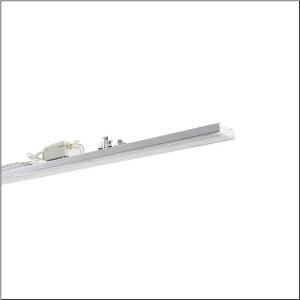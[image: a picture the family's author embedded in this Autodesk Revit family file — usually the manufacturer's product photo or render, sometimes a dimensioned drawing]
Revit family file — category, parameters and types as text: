
# Revit family: licross_r__21_recessed_mo_52tl11mn4a5g_bccd
name_source: partatom
category: Lighting Fixtures
units: mm (PartAtom-declared; Revit-internal decimal feet)

## family parameters
Cut with Voids When Loaded = No
Host = Face
Light Source = No
Part Type = Normal
Room Calculation Point = No
Round Connector Dimension = Use Diameter
Shared = No

## types (1)
- --- (1 x LED, 10830 lm, 60.5 W, 4000K)
    Apparent Load = 61 VA
    CIE Flux Codes = 89 96 99 100 100
    Color Rendering = 80
    Color Temperature = 4000K
    Default Elevation = 1800 mm
    Description = Licross® 21 Recessed MO, luminaire insert, of sheet steel, galvanised, coil coated, white, length: 1.500mm, width: 66mm, height: 67mm, LED rated luminous flux: 10.820lm, light colour: 840, control gear: ON/OFF Multilumen, with plug, 3-pole, with phase selection, mains connection: 220..240V, AC, 50/60Hz, rated input power: 61W, halogen-free wiring, primary light control with lens, of plastic, primary optical cover: cover, of PMMA, light emission: direct distribution, primary light characteristic: symmetric, protection rating (complete): IP40, insulation class (complete): insulation class I (protective earthing), certification: CE, ENEC, VDE, UKCA, protection symbol: D if used in an environment without relevant dust loads with corresponding accessories, impact resistance: IK06, permissible ambient temperature for indoor applications: -35..+40°C, corresponds to IFS (International Featured Standards) requirements for safety and quality in the food industry, reducing of maximum allowable ambient temperature of 5°C with ceiling mounting, LABS conformity tested according to VDMA 24364:2018-05, packaging unit: 1 piece
    Height = 58 mm
    Lamp = 1 x LED
    Lamp Light Flux = 10830 lm
    Lamp Power = 60.5 W
    Lamp count = 1
    Length = 1500 mm
    Luminous efficacy = 179 lm/W
    Manufacturer = Siteco
    ModVariant = No
    Model = 52TL11MN4A5G
    Mounting Place = Ceiling
    Mounting Type = Pendant
    Number of Poles = 1
    OnlyDefault = Yes
    Power Factor = 1
    Product Name = Licross® 21 Recessed MO
    Product group = luminaire insert
    ProductGroupID = 901
    Protection Class = Protection class I
    Protection Degree = IP 40
    RLX_Detail_Level = 1
    RLX_Emergency_Light_Flux = 0 lm
    RLX_Emergency_Type = 0
    RLX_Emergency_Type_DB = No
    RlxData = <blob elided: 22169 chars, md5=3a20e823>
    Socket = socket
    Standby Power = 0 W
    System Light Flux = 10830 lm
    System Power = 61 W
    Type Comments = factory setting: luminous flux: 100 % | (A | C | E) | 140 mA
    Type Image = l_1296930.jpg
    URL = http://relux.com
    VarID = @adj_038161
    Voltage = 0 V
    Weight = 0.00 kg
    Width = 66 mm

## geometry (parser evidence)
native form markers: Blend x4, Sweep x11
no freeform markers — native parametric forms only
